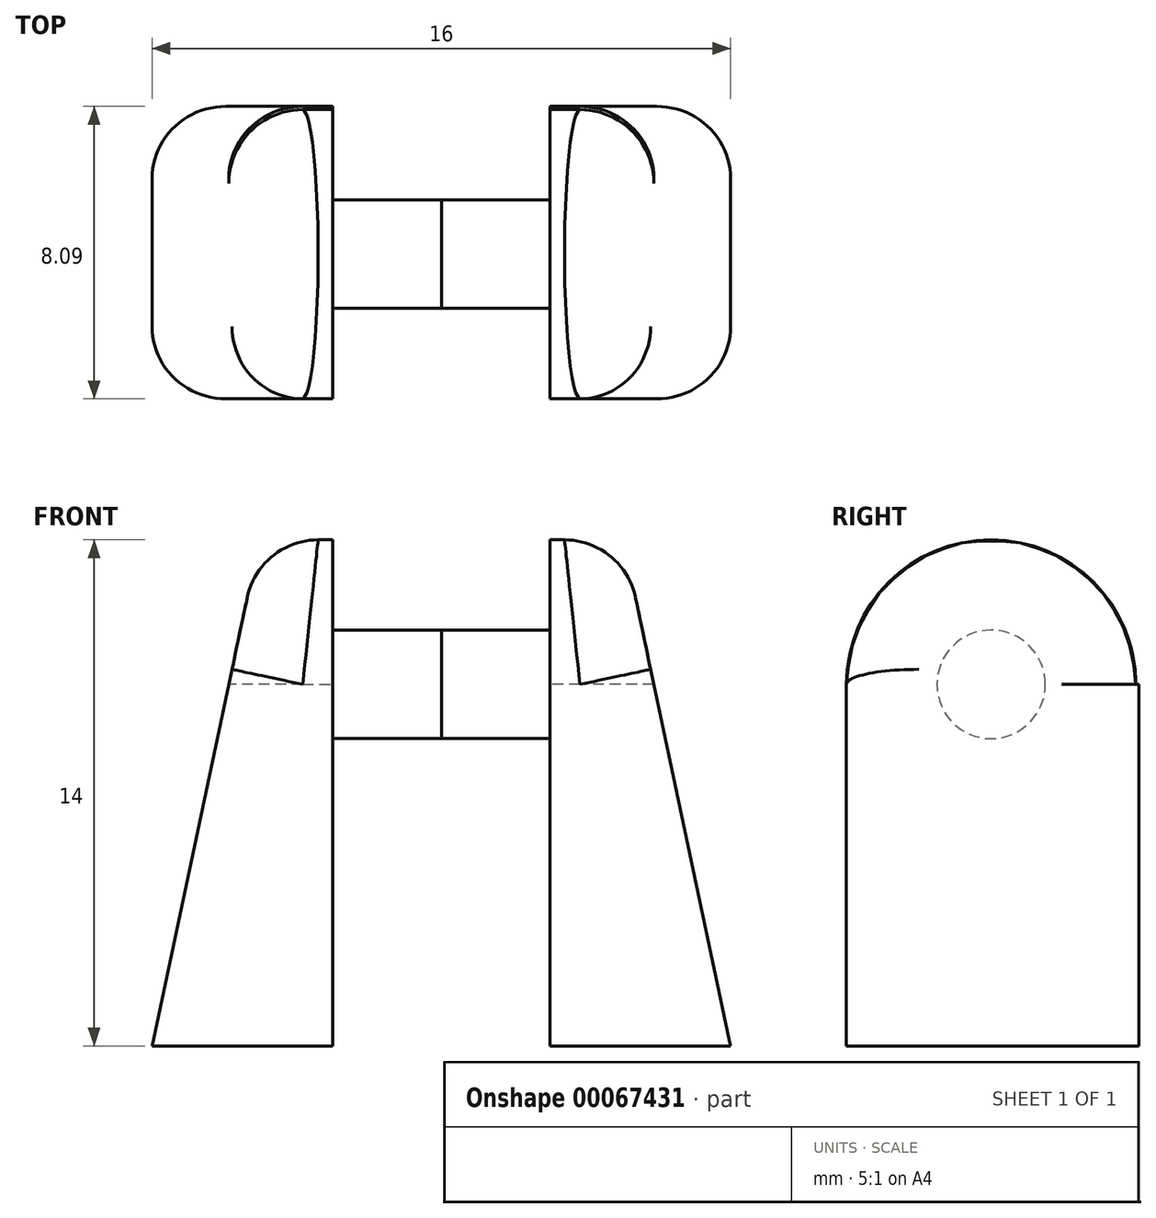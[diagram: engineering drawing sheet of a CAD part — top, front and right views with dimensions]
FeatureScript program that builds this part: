
annotation { "Feature Type Name" : "Feature", "Feature Type Description" : "" }
export const myFeature = defineFeature(function(context is Context, id is Id, definition is map)
    precondition{}
    {
        {
            var Q0;
            Q0=qCreatedBy(makeId("Right.planeOp"),FACE);
            var sketch = newSketch(context, id + "F0", { "sketchPlane" : qUnion([Q0])});
            skCircle(sketch, "E0", {"center": v(0, 0) * mm, "radius": 1.5 * mm});
            skSolve(sketch);
        }
        {
            var Q0;
            Q0=qSketchRegion(id+"F0",true);
            extrude(context, id + "F1", {"entities" : qUnion([Q0]), "depth" : 3 * mm});
        }
        {
            var Q0;
            Q0=makeQuery(id+"F1.opExtrude","CAP_FACE",FACE,{"disambiguationData":[OSD([sQuery(id+"F0.wireOp",EDGE,"E0")])],"isStart":false});
            var sketch = newSketch(context, id + "F2", { "sketchPlane" : qUnion([Q0])});
            skArc(sketch, "E1", {"start": v(4, 0) * mm, "mid": v(0, 4) * mm, "end": v(-4, 0) * mm});
            skLineSegment(sketch, "E2.bottom", {"start": v(4, 0) * mm, "end": v(4.09, 0) * mm});
            skLineSegment(sketch, "E2.top", {"start": v(-4, -10) * mm, "end": v(4.09, -10) * mm});
            skLineSegment(sketch, "E2.left", {"start": v(-4, 0) * mm, "end": v(-4, -10) * mm});
            skLineSegment(sketch, "E2.right", {"start": v(4.09, 0) * mm, "end": v(4.09, -10) * mm});
            skLineSegment(sketch, "E3", {"start": v(4.09, -10) * mm, "end": v(0.56, -16.47) * mm, "construction": true});
            skLineSegment(sketch, "E4", {"start": v(0.56, -16.47) * mm, "end": v(-5.68, -13.07) * mm, "construction": true});
            skLineSegment(sketch, "E5", {"start": v(-5.68, -13.07) * mm, "end": v(-4, -10) * mm, "construction": true});
            skLineSegment(sketch, "E6", {"start": v(-2.56, -14.77) * mm, "end": v(-1.11, -12.12) * mm, "construction": true});
            skSolve(sketch);
        }
        {
            var Q0;
            Q0=qSketchRegion(id+"F2",true);
            extrude(context, id + "F3", {"entities" : qUnion([Q0]), "operationType" : NewBodyOperationType.ADD, "depth" : 5 * mm});
        }
        {
            var Q0;
            Q0=makeQuery(id+"F3.opExtrude","SWEPT_FACE",FACE,{"disambiguationData":[OSD([sQuery(id+"F2.wireOp",EDGE,"E2.left")])]});
            var sketch = newSketch(context, id + "F4", { "sketchPlane" : qUnion([Q0])});
            skLineSegment(sketch, "E7", {"start": v(8, -10) * mm, "end": v(4.67, 5.66) * mm});
            skLineSegment(sketch, "E8", {"start": v(4.67, 5.66) * mm, "end": v(9.49, 5.66) * mm});
            skLineSegment(sketch, "E9", {"start": v(9.49, 5.66) * mm, "end": v(8, -10) * mm});
            skSolve(sketch);
        }
        {
            var Q0;
            Q0=qSketchRegion(id+"F4",true);
            extrude(context, id + "F5", {"entities" : qUnion([Q0]), "operationType" : NewBodyOperationType.REMOVE, "oppositeDirection" : true, "depth" : 25 * mm});
        }
        {
            var Q0;
            Q0=makeQuery(id+"F5.boolean.opBoolean","COPY",EDGE,{"derivedFrom":makeQuery(id+"F5.opExtrude","CAP_EDGE",EDGE,{"disambiguationData":[OSD([sQuery(id+"F4.wireOp",EDGE,"E7")])],"isStart":true})});
            var Q1;
            Q1=makeQuery(id+"F5.boolean.opBoolean","INTERSECT",EDGE,{"derivedFrom":[makeQuery(id+"F3.opExtrude","SWEPT_FACE",FACE,{"disambiguationData":[OSD([sQuery(id+"F2.wireOp",EDGE,"E1")])]}),makeQuery(id+"F5.opExtrude","SWEPT_FACE",FACE,{"disambiguationData":[OSD([sQuery(id+"F4.wireOp",EDGE,"E7")])]})]});
            fillet(context, id + "F6", {"entities" : qUnion([Q0, Q1]), "radius" : 2 * mm, "tangentPropagation" : true, "allowEdgeOverflow" : false});
        }
        {
            var Q0;
            Q0=makeQuery(id+"F5.boolean.opBoolean","INTERSECT",EDGE,{"derivedFrom":[makeQuery(id+"F3.opExtrude","SWEPT_FACE",FACE,{"disambiguationData":[OSD([sQuery(id+"F2.wireOp",EDGE,"E2.right")])]}),makeQuery(id+"F5.opExtrude","SWEPT_FACE",FACE,{"disambiguationData":[OSD([sQuery(id+"F4.wireOp",EDGE,"E7")])]})]});
            fillet(context, id + "F7", {"entities" : qUnion([Q0]), "radius" : 2 * mm, "tangentPropagation" : true, "allowEdgeOverflow" : false});
        }
        {
            var Q0;
            Q0=makeQuery(id+"F1.opExtrude","SWEPT_BODY",BODY,{"disambiguationData":[OSD([sQuery(id+"F0.wireOp",EDGE,"E0")])]});
            var Q1;
            Q1=makeQuery(id+"F1.opExtrude","CAP_FACE",FACE,{"disambiguationData":[OSD([sQuery(id+"F0.wireOp",EDGE,"E0")])],"isStart":true});
            mirror(context, id + "F8", {"entities" : qUnion([Q0]), "mirrorPlane" : qUnion([Q1])});
        }
    });
